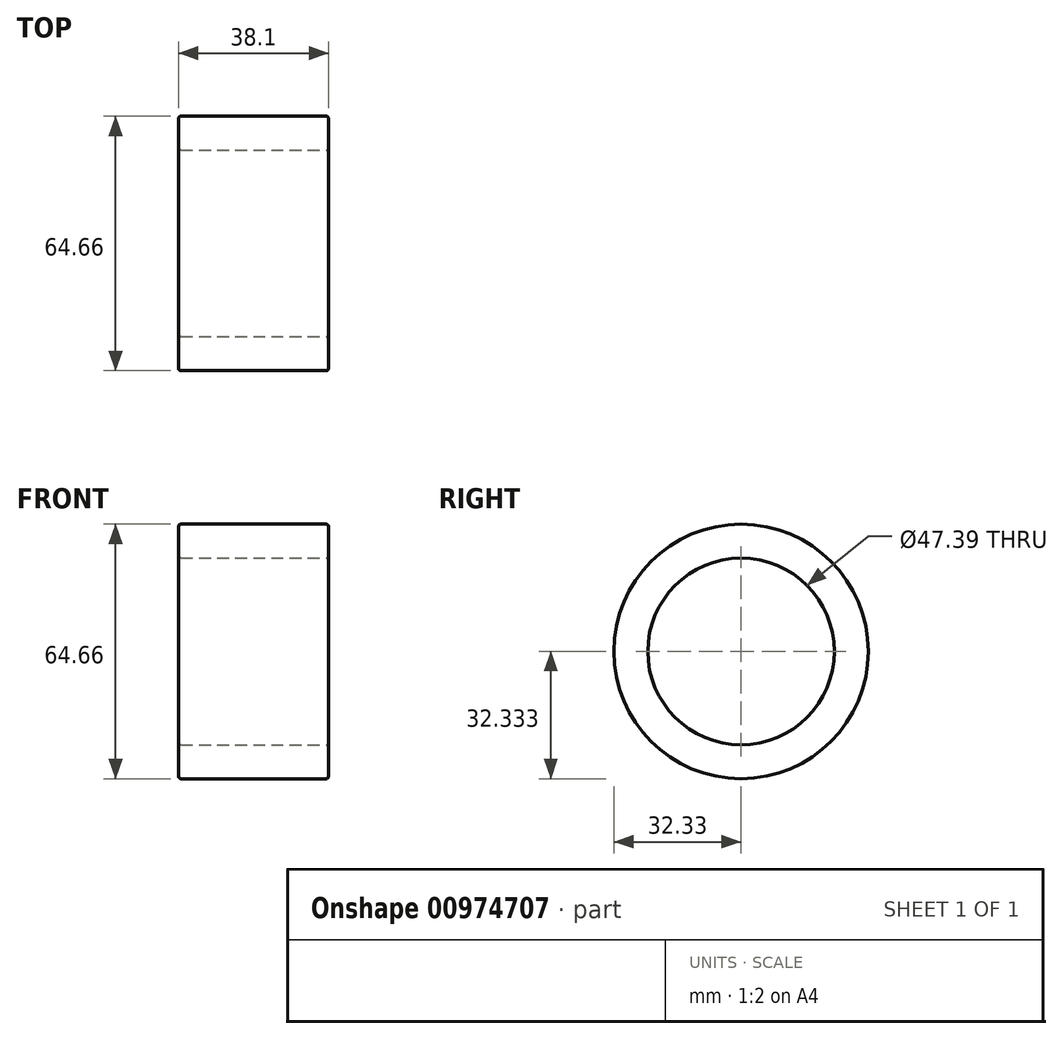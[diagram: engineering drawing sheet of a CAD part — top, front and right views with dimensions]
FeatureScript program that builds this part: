
annotation { "Feature Type Name" : "Feature", "Feature Type Description" : "" }
export const myFeature = defineFeature(function(context is Context, id is Id, definition is map)
    precondition{}
    {
        {
            var Q0;
            Q0=qCreatedBy(makeId("Top.planeOp"),FACE);
            var sketch = newSketch(context, id + "F0", { "sketchPlane" : qUnion([Q0])});
            skLineSegment(sketch, "E0.bottom", {"start": v(-25.4, 25.4) * mm, "end": v(12.7, 25.4) * mm});
            skLineSegment(sketch, "E0.top", {"start": v(-25.4, -12.7) * mm, "end": v(12.7, -12.7) * mm});
            skLineSegment(sketch, "E0.left", {"start": v(-25.4, 25.4) * mm, "end": v(-25.4, -12.7) * mm});
            skLineSegment(sketch, "E0.right", {"start": v(12.7, 25.4) * mm, "end": v(12.7, -12.7) * mm});
            skSolve(sketch);
        }
        {
            var Q0;
            Q0=qCreatedBy(makeId("Right.planeOp"),FACE);
            var sketch = newSketch(context, id + "F1", { "sketchPlane" : qUnion([Q0])});
            skCircle(sketch, "E1", {"center": v(0, 20) * mm, "radius": 12.7 * mm});
            skSolve(sketch);
        }
        {
            var Q0;
            Q0=makeQuery(id+"F0.imprint","IMPRINT",FACE,{"disambiguationData":[TD([[makeQuery(id+"F0.imprint","IMPRINT",EDGE,{"derivedFrom":sQuery(id+"F0.wireOp",EDGE,"E0.bottom")}),-1.0]])]});
            var Q1;
            Q1=sQuery(id+"F1.wireOp",EDGE,"E1");
            sweep(context, id + "F2", {"profiles" : qUnion([Q0]), "path" : qUnion([Q1])});
        }
        {
            var Q0;
            Q0=makeQuery(id+"F2.opSweep","SWEPT_EDGE",EDGE,{"disambiguationData":[OSD([sQuery(id+"F0.wireOp",EDGE,"E0.top"),sQuery(id+"F0.wireOp",EDGE,"E0.right"),sQuery(id+"F1.wireOp",EDGE,"E1")])]});
            var Q1;
            Q1=makeQuery(id+"F2.opSweep","SWEPT_EDGE",EDGE,{"disambiguationData":[OSD([sQuery(id+"F0.wireOp",EDGE,"E0.bottom"),sQuery(id+"F0.wireOp",EDGE,"E0.right"),sQuery(id+"F1.wireOp",EDGE,"E1")])]});
            var Q2;
            Q2=makeQuery(id+"F2.opSweep","SWEPT_FACE",FACE,{"disambiguationData":[OSD([sQuery(id+"F0.wireOp",EDGE,"E0.left"),sQuery(id+"F1.wireOp",EDGE,"E1")])]});
            var Q3;
            Q3=makeQuery(id+"F2.opSweep","SWEPT_EDGE",EDGE,{"disambiguationData":[OSD([sQuery(id+"F0.wireOp",EDGE,"E0.top"),sQuery(id+"F0.wireOp",EDGE,"E0.left"),sQuery(id+"F1.wireOp",EDGE,"E1")])]});
            fillet(context, id + "F3", {"entities" : qUnion([Q0, Q1, Q2, Q3]), "radius" : 0.61 * mm, "tangentPropagation" : true, "allowEdgeOverflow" : false});
        }
    });
